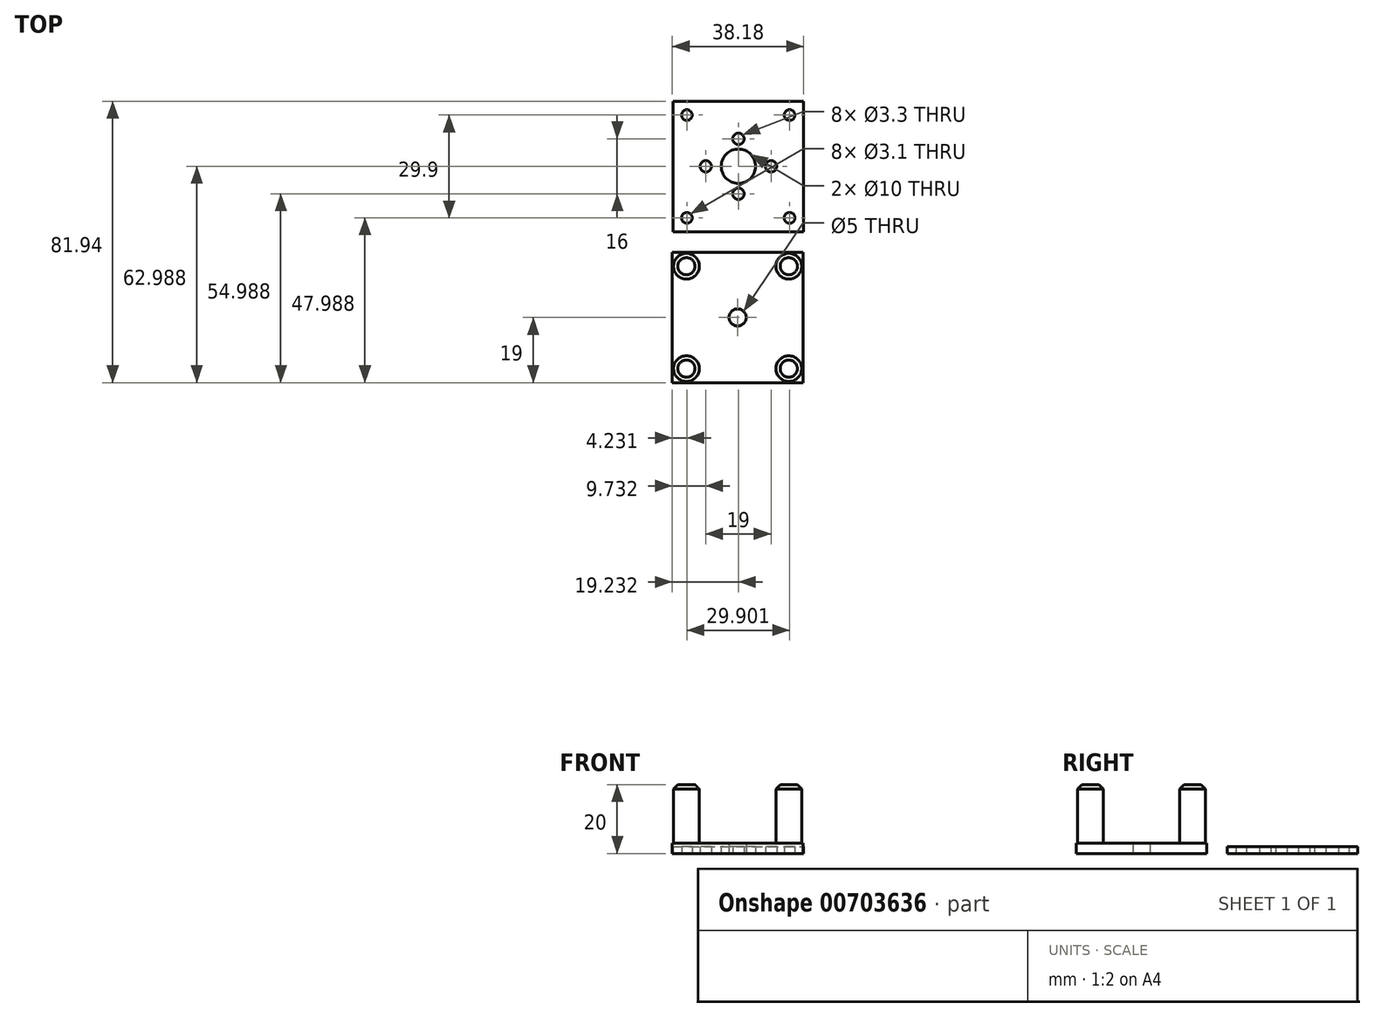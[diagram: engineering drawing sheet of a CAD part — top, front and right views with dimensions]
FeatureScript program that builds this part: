
annotation { "Feature Type Name" : "Feature", "Feature Type Description" : "" }
export const myFeature = defineFeature(function(context is Context, id is Id, definition is map)
    precondition{}
    {
        {
            var Q0;
            Q0=qCreatedBy(makeId("Top.planeOp"),FACE);
            var sketch = newSketch(context, id + "F0", { "sketchPlane" : qUnion([Q0])});
            skLineSegment(sketch, "E0.bottom", {"start": v(0, 0) * mm, "end": v(38, 0) * mm});
            skLineSegment(sketch, "E0.top", {"start": v(0, -38) * mm, "end": v(38, -38) * mm});
            skLineSegment(sketch, "E0.left", {"start": v(0, 0) * mm, "end": v(0, -38) * mm});
            skLineSegment(sketch, "E0.right", {"start": v(38, 0) * mm, "end": v(38, -38) * mm});
            skLineSegment(sketch, "E1", {"start": v(19, 0) * mm, "end": v(19, -38) * mm, "construction": true});
            skLineSegment(sketch, "E2", {"start": v(0, -19) * mm, "end": v(38, -19) * mm, "construction": true});
            skCircle(sketch, "E3", {"center": v(19, -19) * mm, "radius": 2.5 * mm});
            skLineSegment(sketch, "E4.0", {"start": v(1, -1) * mm, "end": v(37, -1) * mm, "construction": true});
            skLineSegment(sketch, "E4.1", {"start": v(1, -1) * mm, "end": v(1, -37) * mm, "construction": true});
            skLineSegment(sketch, "E4.2", {"start": v(1, -37) * mm, "end": v(37, -37) * mm, "construction": true});
            skLineSegment(sketch, "E4.3", {"start": v(37, -1) * mm, "end": v(37, -37) * mm, "construction": true});
            skLineSegment(sketch, "E5", {"start": v(1, -1) * mm, "end": v(4.17, -1) * mm, "construction": true});
            skLineSegment(sketch, "E6", {"start": v(1, -1) * mm, "end": v(1, -4.03) * mm, "construction": true});
            skCircle(sketch, "E7", {"center": v(4.1, -4.1) * mm, "radius": 1.4 * mm});
            skLineSegment(sketch, "E8", {"start": v(33.9, -1) * mm, "end": v(33.9, -4.1) * mm, "construction": true});
            skLineSegment(sketch, "E9", {"start": v(33.9, -4.1) * mm, "end": v(37, -4.1) * mm, "construction": true});
            skCircle(sketch, "E10", {"center": v(33.9, -4.1) * mm, "radius": 1.4 * mm});
            skLineSegment(sketch, "E11", {"start": v(33.9, -37) * mm, "end": v(33.9, -33.9) * mm, "construction": true});
            skLineSegment(sketch, "E12", {"start": v(33.9, -33.9) * mm, "end": v(37, -33.9) * mm, "construction": true});
            skLineSegment(sketch, "E13", {"start": v(1, -33.9) * mm, "end": v(4.1, -33.9) * mm, "construction": true});
            skLineSegment(sketch, "E14", {"start": v(4.1, -33.9) * mm, "end": v(4.1, -37) * mm, "construction": true});
            skCircle(sketch, "E15", {"center": v(4.1, -33.9) * mm, "radius": 1.4 * mm});
            skCircle(sketch, "E16", {"center": v(33.9, -33.9) * mm, "radius": 1.4 * mm});
            skLineSegment(sketch, "E17", {"start": v(4.17, -1) * mm, "end": v(4.1, -4.1) * mm, "construction": true});
            skLineSegment(sketch, "E18", {"start": v(1, -4.03) * mm, "end": v(4.1, -4.1) * mm, "construction": true});
            skPoint(sketch, "E19", {"position": v(4.13, -2.7) * mm});
            skPoint(sketch, "E20", {"position": v(2.7, -4.07) * mm});
            skPoint(sketch, "E21", {"position": v(33.9, -2.7) * mm});
            skPoint(sketch, "E22", {"position": v(35.3, -4.1) * mm});
            skLineSegment(sketch, "E23", {"start": v(4.1, -4.1) * mm, "end": v(33.9, -4.1) * mm, "construction": true});
            skPoint(sketch, "E24", {"position": v(5.5, -4.1) * mm});
            skPoint(sketch, "E25", {"position": v(32.5, -4.1) * mm});
            skPoint(sketch, "E26", {"position": v(2.7, -33.9) * mm});
            skPoint(sketch, "E27", {"position": v(4.1, -35.3) * mm});
            skPoint(sketch, "E28", {"position": v(33.9, -35.3) * mm});
            skPoint(sketch, "E29", {"position": v(35.3, -33.9) * mm});
            skLineSegment(sketch, "E30", {"start": v(4.1, -33.9) * mm, "end": v(33.9, -33.9) * mm, "construction": true});
            skPoint(sketch, "E31", {"position": v(5.5, -33.9) * mm});
            skPoint(sketch, "E32", {"position": v(32.5, -33.9) * mm});
            skLineSegment(sketch, "E33", {"start": v(33.9, -4.1) * mm, "end": v(33.9, -33.9) * mm, "construction": true});
            skLineSegment(sketch, "E34", {"start": v(4.1, -4.1) * mm, "end": v(4.1, -33.9) * mm, "construction": true});
            skPoint(sketch, "E35", {"position": v(4.1, -5.5) * mm});
            skPoint(sketch, "E36", {"position": v(4.1, -32.5) * mm});
            skPoint(sketch, "E37", {"position": v(33.9, -32.5) * mm});
            skPoint(sketch, "E38", {"position": v(33.9, -5.5) * mm});
            skCircle(sketch, "E39", {"center": v(19.23, 24.99) * mm, "radius": 5 * mm});
            skLineSegment(sketch, "E40", {"start": v(19.23, 24.99) * mm, "end": v(9.73, 24.99) * mm, "construction": true});
            skLineSegment(sketch, "E41", {"start": v(19.23, 24.99) * mm, "end": v(19.23, 32.99) * mm, "construction": true});
            skLineSegment(sketch, "E42", {"start": v(19.23, 24.99) * mm, "end": v(19.23, 16.99) * mm, "construction": true});
            skLineSegment(sketch, "E43", {"start": v(19.23, 24.99) * mm, "end": v(28.73, 24.99) * mm, "construction": true});
            skCircle(sketch, "E44", {"center": v(19.23, 32.99) * mm, "radius": 1.65 * mm});
            skCircle(sketch, "E45", {"center": v(28.73, 24.99) * mm, "radius": 1.65 * mm});
            skCircle(sketch, "E46", {"center": v(19.23, 16.99) * mm, "radius": 1.65 * mm});
            skCircle(sketch, "E47", {"center": v(9.73, 24.99) * mm, "radius": 1.65 * mm});
            skLineSegment(sketch, "E48.bottom", {"start": v(0.18, 43.94) * mm, "end": v(38.18, 43.94) * mm});
            skLineSegment(sketch, "E48.top", {"start": v(0.18, 5.94) * mm, "end": v(38.18, 5.94) * mm});
            skLineSegment(sketch, "E48.left", {"start": v(0.18, 43.94) * mm, "end": v(0.18, 5.94) * mm});
            skLineSegment(sketch, "E48.right", {"start": v(38.18, 43.94) * mm, "end": v(38.18, 5.94) * mm});
            skLineSegment(sketch, "E49", {"start": v(19.18, 43.94) * mm, "end": v(19.18, 5.94) * mm, "construction": true});
            skLineSegment(sketch, "E50", {"start": v(0.18, 24.94) * mm, "end": v(38.18, 24.94) * mm, "construction": true});
            skLineSegment(sketch, "E51.0", {"start": v(1.18, 42.94) * mm, "end": v(37.18, 42.94) * mm, "construction": true});
            skLineSegment(sketch, "E51.1", {"start": v(1.18, 42.94) * mm, "end": v(1.18, 6.94) * mm, "construction": true});
            skLineSegment(sketch, "E51.2", {"start": v(1.18, 6.94) * mm, "end": v(37.18, 6.94) * mm, "construction": true});
            skLineSegment(sketch, "E51.3", {"start": v(37.18, 42.94) * mm, "end": v(37.18, 6.94) * mm, "construction": true});
            skLineSegment(sketch, "E52", {"start": v(1.18, 42.94) * mm, "end": v(4.3, 42.94) * mm, "construction": true});
            skLineSegment(sketch, "E53", {"start": v(1.18, 42.94) * mm, "end": v(1.18, 39.96) * mm, "construction": true});
            skCircle(sketch, "E54", {"center": v(4.23, 39.89) * mm, "radius": 1.55 * mm});
            skLineSegment(sketch, "E55", {"start": v(34.13, 42.94) * mm, "end": v(34.13, 39.89) * mm, "construction": true});
            skLineSegment(sketch, "E56", {"start": v(34.13, 39.89) * mm, "end": v(37.18, 39.89) * mm, "construction": true});
            skCircle(sketch, "E57", {"center": v(34.13, 39.89) * mm, "radius": 1.55 * mm});
            skLineSegment(sketch, "E58", {"start": v(34.13, 6.94) * mm, "end": v(34.13, 9.99) * mm, "construction": true});
            skLineSegment(sketch, "E59", {"start": v(34.13, 9.99) * mm, "end": v(37.18, 9.99) * mm, "construction": true});
            skLineSegment(sketch, "E60", {"start": v(1.18, 9.99) * mm, "end": v(4.23, 9.99) * mm, "construction": true});
            skLineSegment(sketch, "E61", {"start": v(4.23, 9.99) * mm, "end": v(4.23, 6.94) * mm, "construction": true});
            skCircle(sketch, "E62", {"center": v(4.23, 9.99) * mm, "radius": 1.55 * mm});
            skCircle(sketch, "E63", {"center": v(34.13, 9.99) * mm, "radius": 1.55 * mm});
            skLineSegment(sketch, "E64", {"start": v(4.3, 42.94) * mm, "end": v(4.23, 39.89) * mm, "construction": true});
            skLineSegment(sketch, "E65", {"start": v(1.18, 39.96) * mm, "end": v(4.23, 39.89) * mm, "construction": true});
            skPoint(sketch, "E66", {"position": v(4.27, 41.44) * mm});
            skPoint(sketch, "E67", {"position": v(2.68, 39.93) * mm});
            skPoint(sketch, "E68", {"position": v(34.13, 41.44) * mm});
            skPoint(sketch, "E69", {"position": v(35.68, 39.89) * mm});
            skLineSegment(sketch, "E70", {"start": v(4.23, 39.89) * mm, "end": v(34.13, 39.89) * mm, "construction": true});
            skPoint(sketch, "E71", {"position": v(5.78, 39.89) * mm});
            skPoint(sketch, "E72", {"position": v(32.58, 39.89) * mm});
            skPoint(sketch, "E73", {"position": v(2.68, 9.99) * mm});
            skPoint(sketch, "E74", {"position": v(4.23, 8.44) * mm});
            skPoint(sketch, "E75", {"position": v(34.13, 8.44) * mm});
            skPoint(sketch, "E76", {"position": v(35.68, 9.99) * mm});
            skLineSegment(sketch, "E77", {"start": v(4.23, 9.99) * mm, "end": v(34.13, 9.99) * mm, "construction": true});
            skPoint(sketch, "E78", {"position": v(5.78, 9.99) * mm});
            skPoint(sketch, "E79", {"position": v(32.58, 9.99) * mm});
            skLineSegment(sketch, "E80", {"start": v(34.13, 39.89) * mm, "end": v(34.13, 9.99) * mm, "construction": true});
            skLineSegment(sketch, "E81", {"start": v(4.23, 39.89) * mm, "end": v(4.23, 9.99) * mm, "construction": true});
            skPoint(sketch, "E82", {"position": v(4.23, 38.34) * mm});
            skPoint(sketch, "E83", {"position": v(4.23, 11.54) * mm});
            skPoint(sketch, "E84", {"position": v(34.13, 11.54) * mm});
            skPoint(sketch, "E85", {"position": v(34.13, 38.34) * mm});
            skPoint(sketch, "E86", {"position": v(16.83, 24.99) * mm});
            skCircle(sketch, "E87", {"center": v(4.1, -4.1) * mm, "radius": 3.75 * mm});
            skCircle(sketch, "E88", {"center": v(33.9, -4.1) * mm, "radius": 3.75 * mm});
            skCircle(sketch, "E89", {"center": v(33.9, -33.9) * mm, "radius": 3.75 * mm});
            skCircle(sketch, "E90", {"center": v(4.1, -33.9) * mm, "radius": 3.75 * mm});
            skSolve(sketch);
        }
        {
            var Q0;
            Q0=makeQuery(id+"F0.imprint","IMPRINT",FACE,{"disambiguationData":[TD([[makeQuery(id+"F0.imprint","IMPRINT",EDGE,{"derivedFrom":sQuery(id+"F0.wireOp",EDGE,"E39")}),-1.0]])]});
            extrude(context, id + "F1", {"entities" : qUnion([Q0]), "depth" : 2 * mm, "offsetDistance" : 25 * mm});
        }
        {
            var Q0;
            Q0=makeQuery(id+"F0.imprint","IMPRINT",FACE,{"disambiguationData":[TD([[makeQuery(id+"F0.imprint","IMPRINT",EDGE,{"derivedFrom":sQuery(id+"F0.wireOp",EDGE,"E0.bottom")}),-1.0]])]});
            extrude(context, id + "F2", {"entities" : qUnion([Q0]), "depth" : 3 * mm, "offsetDistance" : 25 * mm});
        }
        {
            var Q0;
            Q0=makeQuery(id+"F0.imprint","IMPRINT",FACE,{"disambiguationData":[TD([[makeQuery(id+"F0.imprint","IMPRINT",EDGE,{"derivedFrom":sQuery(id+"F0.wireOp",EDGE,"E16")}),1.0]])]});
            var Q1;
            Q1=makeQuery(id+"F0.imprint","IMPRINT",FACE,{"disambiguationData":[TD([[makeQuery(id+"F0.imprint","IMPRINT",EDGE,{"derivedFrom":sQuery(id+"F0.wireOp",EDGE,"E15")}),1.0]])]});
            var Q2;
            Q2=makeQuery(id+"F0.imprint","IMPRINT",FACE,{"disambiguationData":[TD([[makeQuery(id+"F0.imprint","IMPRINT",EDGE,{"derivedFrom":sQuery(id+"F0.wireOp",EDGE,"E7")}),1.0]])]});
            var Q3;
            Q3=makeQuery(id+"F0.imprint","IMPRINT",FACE,{"disambiguationData":[TD([[makeQuery(id+"F0.imprint","IMPRINT",EDGE,{"derivedFrom":sQuery(id+"F0.wireOp",EDGE,"E10")}),1.0]])]});
            extrude(context, id + "F3", {"entities" : qUnion([Q0, Q1, Q2, Q3]), "operationType" : NewBodyOperationType.ADD, "depth" : 20 * mm, "offsetDistance" : 25 * mm});
        }
        {
            var Q0;
            Q0=makeQuery(id+"F0.imprint","IMPRINT",FACE,{"disambiguationData":[TD([[makeQuery(id+"F0.imprint","IMPRINT",EDGE,{"derivedFrom":sQuery(id+"F0.wireOp",EDGE,"E7")}),-1.0]])]});
            var Q1;
            Q1=makeQuery(id+"F0.imprint","IMPRINT",FACE,{"disambiguationData":[TD([[makeQuery(id+"F0.imprint","IMPRINT",EDGE,{"derivedFrom":sQuery(id+"F0.wireOp",EDGE,"E15")}),-1.0]])]});
            var Q2;
            Q2=makeQuery(id+"F0.imprint","IMPRINT",FACE,{"disambiguationData":[TD([[makeQuery(id+"F0.imprint","IMPRINT",EDGE,{"derivedFrom":sQuery(id+"F0.wireOp",EDGE,"E16")}),-1.0]])]});
            var Q3;
            Q3=makeQuery(id+"F0.imprint","IMPRINT",FACE,{"disambiguationData":[TD([[makeQuery(id+"F0.imprint","IMPRINT",EDGE,{"derivedFrom":sQuery(id+"F0.wireOp",EDGE,"E10")}),-1.0]])]});
            extrude(context, id + "F4", {"entities" : qUnion([Q0, Q1, Q2, Q3]), "operationType" : NewBodyOperationType.ADD, "depth" : 20 * mm, "offsetDistance" : 25 * mm});
        }
        {
            var Q0;
            Q0=makeQuery(id+"F4.opExtrude","CAP_EDGE",EDGE,{"disambiguationData":[OSD([sQuery(id+"F0.wireOp",EDGE,"E87")])],"isStart":false});
            var Q1;
            Q1=makeQuery(id+"F4.opExtrude","CAP_EDGE",EDGE,{"disambiguationData":[OSD([sQuery(id+"F0.wireOp",EDGE,"E88")])],"isStart":false});
            var Q2;
            Q2=makeQuery(id+"F4.opExtrude","CAP_EDGE",EDGE,{"disambiguationData":[OSD([sQuery(id+"F0.wireOp",EDGE,"E89")])],"isStart":false});
            var Q3;
            Q3=makeQuery(id+"F4.opExtrude","CAP_EDGE",EDGE,{"disambiguationData":[OSD([sQuery(id+"F0.wireOp",EDGE,"E90")])],"isStart":false});
            chamfer(context, id + "F5", {"entities" : qUnion([Q0, Q1, Q2, Q3]), "width" : 1.25 * mm, "tangentPropagation" : true});
        }
        {
            var Q0;
            Q0=makeQuery(id+"F0.imprint","IMPRINT",FACE,{"disambiguationData":[TD([[makeQuery(id+"F0.imprint","IMPRINT",EDGE,{"derivedFrom":sQuery(id+"F0.wireOp",EDGE,"E39")}),-1.0]])]});
            extrude(context, id + "F6", {"entities" : qUnion([Q0]), "depth" : 2 * mm, "offsetDistance" : 25 * mm});
        }
    });
